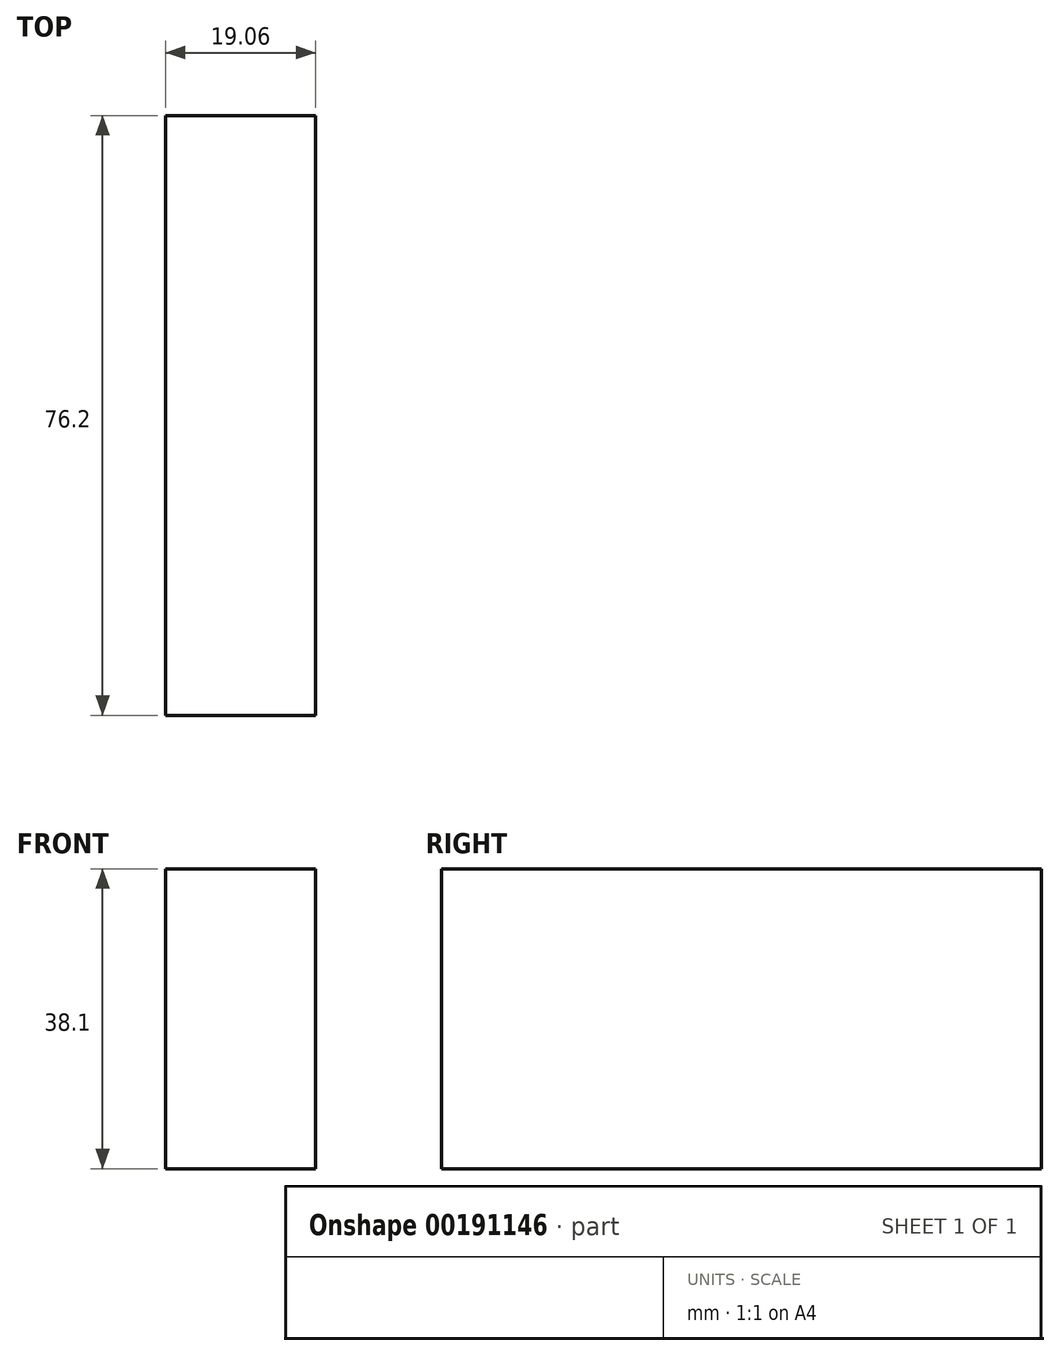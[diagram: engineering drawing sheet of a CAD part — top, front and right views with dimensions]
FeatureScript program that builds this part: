
annotation { "Feature Type Name" : "Feature", "Feature Type Description" : "" }
export const myFeature = defineFeature(function(context is Context, id is Id, definition is map)
    precondition{}
    {
        {
            var Q0;
            Q0=qCreatedBy(makeId("Right.planeOp"),FACE);
            var sketch = newSketch(context, id + "F0", { "sketchPlane" : qUnion([Q0])});
            skLineSegment(sketch, "E0.bottom", {"start": v(-38.1, -19.05) * mm, "end": v(38.1, -19.05) * mm});
            skLineSegment(sketch, "E0.top", {"start": v(-38.1, 19.05) * mm, "end": v(38.1, 19.05) * mm});
            skLineSegment(sketch, "E0.left", {"start": v(-38.1, -19.05) * mm, "end": v(-38.1, 19.05) * mm});
            skLineSegment(sketch, "E0.right", {"start": v(38.1, -19.05) * mm, "end": v(38.1, 19.05) * mm});
            skLineSegment(sketch, "E1", {"start": v(-38.1, -19.05) * mm, "end": v(38.1, 19.05) * mm, "construction": true});
            skPoint(sketch, "E2", {"position": v(0, 0) * mm});
            skSolve(sketch);
        }
        {
            var Q0;
            Q0 = qSketchRegion(id + "F0", true);
            extrude(context, id + "F1", {"entities" : qUnion([Q0]), "endBound" : BoundingType.SYMMETRIC, "depth" : 19.05 * mm});
        }
    });
